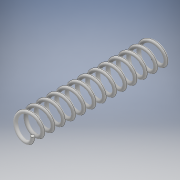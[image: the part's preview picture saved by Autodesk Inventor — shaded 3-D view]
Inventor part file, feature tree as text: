
AUTODESK INVENTOR PART (.ipt)
format: ipt  version: 2018 (Build 220112000, 112)  size: 296,960 bytes
history: native  units: mm
features: helix x1, sketch x1
ambient origin geometry x8: Origin, YZ Plane, XZ Plane, XY Plane, X Axis, Y Axis, Z Axis, Center Point
bodies: Solid1 (feature_tree)
feature tree (2):
  helix  "Coil1"  [1 undecoded]
  sketch  "Sketch1"  dims[d1=0.5mm d2=1.6mm d3=1.5mm d4=20.0mm d5=10.0mm d6=0.0mm d7=90.0deg d8=90.0deg d9=0.0mm d10=0.0mm]
note: 1 required parameter value undecoded (feature->parameter linkage not recoverable at this tier; creation-order binding heuristic only, values carry confidence <= 0.55)
